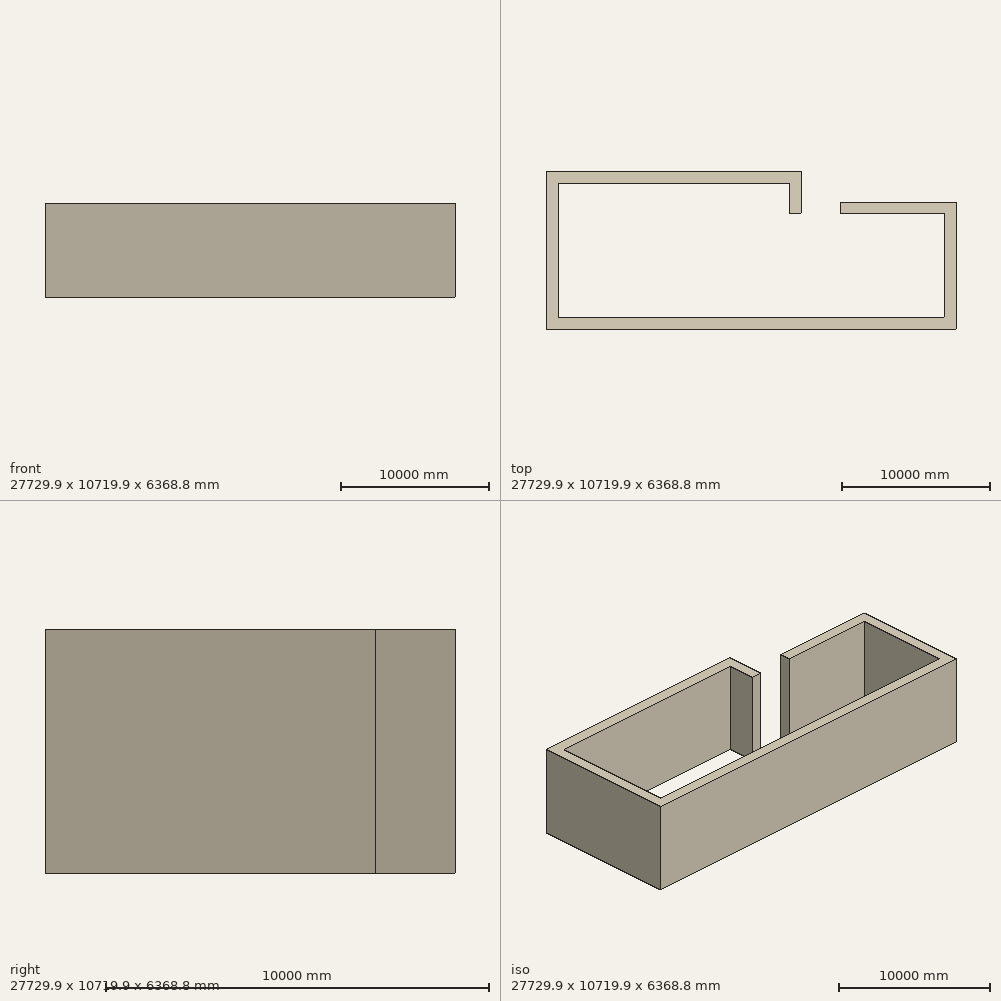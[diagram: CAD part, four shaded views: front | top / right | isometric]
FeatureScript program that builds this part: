
annotation { "Feature Type Name" : "Feature", "Feature Type Description" : "" }
export const myFeature = defineFeature(function(context is Context, id is Id, definition is map)
    precondition{}
    {
        {
            var Q0;
            Q0=qCreatedBy(makeId("Top.planeOp"),FACE);
            var sketch = newSketch(context, id + "F0", { "sketchPlane" : qUnion([Q0])});
            skLineSegment(sketch, "E0", {"start": v(-13072.12, -7698.93) * mm, "end": v(13047.88, -7698.93) * mm});
            skLineSegment(sketch, "E1", {"start": v(13047.88, -7698.93) * mm, "end": v(13047.88, -668.93) * mm});
            skLineSegment(sketch, "E2", {"start": v(13047.88, -668.93) * mm, "end": v(6025, -668.93) * mm});
            skLineSegment(sketch, "E3", {"start": v(2548.25, -668.93) * mm, "end": v(2548.25, 1411.07) * mm});
            skLineSegment(sketch, "E4", {"start": v(2548.25, 1411.07) * mm, "end": v(-13072.12, 1411.07) * mm});
            skLineSegment(sketch, "E5", {"start": v(-13072.12, 1411.07) * mm, "end": v(-13072.12, -7698.93) * mm});
            skLineSegment(sketch, "E6.0", {"start": v(3353.2, 136.03) * mm, "end": v(3353.2, 2216.03) * mm});
            skLineSegment(sketch, "E6.1", {"start": v(-13877.08, 2216.03) * mm, "end": v(-13877.08, -8503.9) * mm});
            skLineSegment(sketch, "E6.2", {"start": v(-13877.08, -8503.9) * mm, "end": v(13852.85, -8503.9) * mm});
            skLineSegment(sketch, "E6.3", {"start": v(3353.2, 2216.03) * mm, "end": v(-13877.08, 2216.03) * mm});
            skLineSegment(sketch, "E6.4", {"start": v(13852.85, -8503.9) * mm, "end": v(13852.85, 136.03) * mm});
            skLineSegment(sketch, "E6.5", {"start": v(13852.85, 136.03) * mm, "end": v(6025, 136.03) * mm});
            skLineSegment(sketch, "E7", {"start": v(3353.2, 136.03) * mm, "end": v(3353.2, -668.93) * mm});
            skLineSegment(sketch, "E8", {"start": v(6025, 136.03) * mm, "end": v(6025, -668.93) * mm});
            skLineSegment(sketch, "E9.trimOffspring", {"start": v(3353.2, -668.93) * mm, "end": v(2548.25, -668.93) * mm});
            skSolve(sketch);
        }
        {
            var Q0;
            Q0 = qSketchRegion(id + "F0", true);
            extrude(context, id + "F1", {"entities" : qUnion([Q0]), "depth" : 6368.8 * mm});
        }
    });
